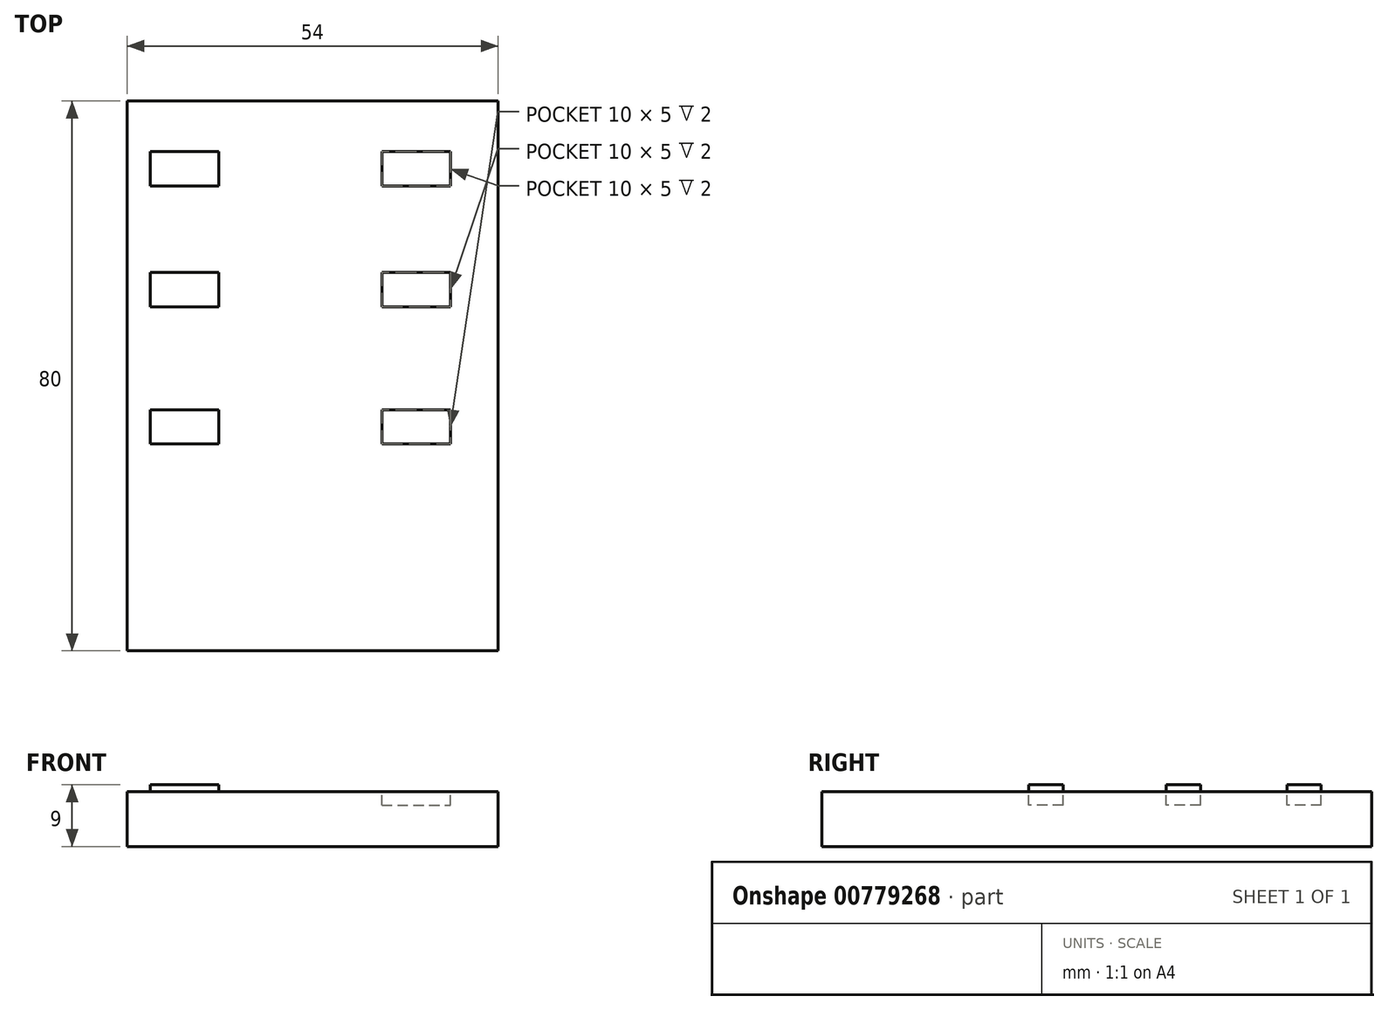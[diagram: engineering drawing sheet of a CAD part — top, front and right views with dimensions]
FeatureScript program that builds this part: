
annotation { "Feature Type Name" : "Feature", "Feature Type Description" : "" }
export const myFeature = defineFeature(function(context is Context, id is Id, definition is map)
    precondition{}
    {
        {
            var Q0;
            Q0=qCreatedBy(makeId("Top.planeOp"),FACE);
            var sketch = newSketch(context, id + "F0", { "sketchPlane" : qUnion([Q0])});
            skLineSegment(sketch, "E0.bottom", {"start": v(27, 40) * mm, "end": v(-27, 40) * mm});
            skLineSegment(sketch, "E0.top", {"start": v(27, -40) * mm, "end": v(-27, -40) * mm});
            skLineSegment(sketch, "E0.left", {"start": v(27, 40) * mm, "end": v(27, -40) * mm});
            skLineSegment(sketch, "E0.right", {"start": v(-27, 40) * mm, "end": v(-27, -40) * mm});
            skPoint(sketch, "E0.middle", {"position": v(0, 0) * mm});
            skSolve(sketch);
        }
        {
            var Q0;
            Q0=makeQuery(id+"F0.imprint","IMPRINT",FACE,{"disambiguationData":[TD([[makeQuery(id+"F0.imprint","IMPRINT",EDGE,{"derivedFrom":sQuery(id+"F0.wireOp",EDGE,"E0.bottom")}),1.0]])]});
            extrude(context, id + "F1", {"entities" : qUnion([Q0]), "depth" : 8 * mm, "offsetDistance" : 25 * mm});
        }
        {
            var Q0;
            Q0=makeQuery(id+"F1.opExtrude","CAP_FACE",FACE,{"disambiguationData":[OSD([sQuery(id+"F0.wireOp",EDGE,"E0.bottom"),sQuery(id+"F0.wireOp",EDGE,"E0.top"),sQuery(id+"F0.wireOp",EDGE,"E0.left"),sQuery(id+"F0.wireOp",EDGE,"E0.right")])],"isStart":false});
            var sketch = newSketch(context, id + "F2", { "sketchPlane" : qUnion([Q0])});
            skLineSegment(sketch, "E1", {"start": v(-23.65, 32.63) * mm, "end": v(-23.65, 27.63) * mm});
            skLineSegment(sketch, "E2.bottom", {"start": v(-23.65, 32.63) * mm, "end": v(-13.65, 32.63) * mm});
            skLineSegment(sketch, "E2.top", {"start": v(-23.65, 27.63) * mm, "end": v(-13.65, 27.63) * mm});
            skLineSegment(sketch, "E2.right", {"start": v(-13.65, 32.63) * mm, "end": v(-13.65, 27.63) * mm});
            skLineSegment(sketch, "E3.bottom", {"start": v(-23.65, 15.07) * mm, "end": v(-13.65, 15.07) * mm});
            skLineSegment(sketch, "E3.top", {"start": v(-23.65, 10.07) * mm, "end": v(-13.65, 10.07) * mm});
            skLineSegment(sketch, "E3.left", {"start": v(-23.65, 15.07) * mm, "end": v(-23.65, 10.07) * mm});
            skLineSegment(sketch, "E3.right", {"start": v(-13.65, 15.07) * mm, "end": v(-13.65, 10.07) * mm});
            skLineSegment(sketch, "E4.bottom", {"start": v(-23.65, -4.93) * mm, "end": v(-13.65, -4.93) * mm});
            skLineSegment(sketch, "E4.top", {"start": v(-23.65, -9.93) * mm, "end": v(-13.65, -9.93) * mm});
            skLineSegment(sketch, "E4.left", {"start": v(-23.65, -4.93) * mm, "end": v(-23.65, -9.93) * mm});
            skLineSegment(sketch, "E4.right", {"start": v(-13.65, -4.93) * mm, "end": v(-13.65, -9.93) * mm});
            skSolve(sketch);
        }
        {
            var Q0;
            Q0=makeQuery(id+"F2.imprint","IMPRINT",FACE,{"disambiguationData":[TD([[makeQuery(id+"F2.imprint","IMPRINT",EDGE,{"derivedFrom":sQuery(id+"F2.wireOp",EDGE,"E1")}),1.0]])]});
            var Q1;
            Q1=makeQuery(id+"F2.imprint","IMPRINT",FACE,{"disambiguationData":[TD([[makeQuery(id+"F2.imprint","IMPRINT",EDGE,{"derivedFrom":sQuery(id+"F2.wireOp",EDGE,"E3.bottom")}),-1.0]])]});
            var Q2;
            Q2=makeQuery(id+"F2.imprint","IMPRINT",FACE,{"disambiguationData":[TD([[makeQuery(id+"F2.imprint","IMPRINT",EDGE,{"derivedFrom":sQuery(id+"F2.wireOp",EDGE,"E4.bottom")}),-1.0]])]});
            extrude(context, id + "F3", {"entities" : qUnion([Q0, Q1, Q2]), "operationType" : NewBodyOperationType.ADD, "depth" : 1 * mm, "offsetDistance" : 25 * mm});
        }
        {
            var Q0;
            Q0=makeQuery(id+"F1.opExtrude","CAP_FACE",FACE,{"disambiguationData":[OSD([sQuery(id+"F0.wireOp",EDGE,"E0.bottom"),sQuery(id+"F0.wireOp",EDGE,"E0.top"),sQuery(id+"F0.wireOp",EDGE,"E0.left"),sQuery(id+"F0.wireOp",EDGE,"E0.right")])],"isStart":false});
            var sketch = newSketch(context, id + "F4", { "sketchPlane" : qUnion([Q0])});
            skLineSegment(sketch, "E5", {"start": v(10.06, 32.63) * mm, "end": v(20.06, 32.63) * mm});
            skLineSegment(sketch, "E6", {"start": v(20.06, 32.63) * mm, "end": v(20.06, 27.63) * mm});
            skLineSegment(sketch, "E7", {"start": v(10.06, 15.07) * mm, "end": v(20.06, 15.07) * mm});
            skLineSegment(sketch, "E8", {"start": v(10.06, -4.93) * mm, "end": v(20.06, -4.93) * mm});
            skLineSegment(sketch, "E9.top", {"start": v(20.06, 27.63) * mm, "end": v(10.06, 27.63) * mm});
            skLineSegment(sketch, "E9.right", {"start": v(10.06, 32.63) * mm, "end": v(10.06, 27.63) * mm});
            skLineSegment(sketch, "E10.top", {"start": v(20.06, 10.07) * mm, "end": v(10.06, 10.07) * mm});
            skLineSegment(sketch, "E10.right", {"start": v(10.06, 15.07) * mm, "end": v(10.06, 10.07) * mm});
            skPoint(sketch, "E11.firstSnap0", {"position": v(20.06, -3.16) * mm});
            skLineSegment(sketch, "E11.top", {"start": v(20.06, -9.93) * mm, "end": v(10.06, -9.93) * mm});
            skLineSegment(sketch, "E11.right", {"start": v(10.06, -4.93) * mm, "end": v(10.06, -9.93) * mm});
            skPoint(sketch, "E12.orphan", {"position": v(20.06, 40) * mm});
            skLineSegment(sketch, "E13.trimOffspring", {"start": v(20.06, 15.07) * mm, "end": v(20.06, 10.07) * mm});
            skLineSegment(sketch, "E14.trimOffspring", {"start": v(20.06, -3.16) * mm, "end": v(20.06, -9.93) * mm});
            skPoint(sketch, "E15.orphan", {"position": v(20.06, -46.32) * mm});
            skPoint(sketch, "E16.orphan", {"position": v(-27, -4.93) * mm});
            skPoint(sketch, "E17.orphan", {"position": v(-27, 15.07) * mm});
            skPoint(sketch, "E18.orphan", {"position": v(-27, 32.63) * mm});
            skSolve(sketch);
        }
        {
            var Q0;
            Q0 = qSketchRegion(id + "F4", true);
            extrude(context, id + "F5", {"entities" : qUnion([Q0]), "operationType" : NewBodyOperationType.REMOVE, "oppositeDirection" : true, "depth" : 2 * mm, "offsetDistance" : 25 * mm});
        }
    });
